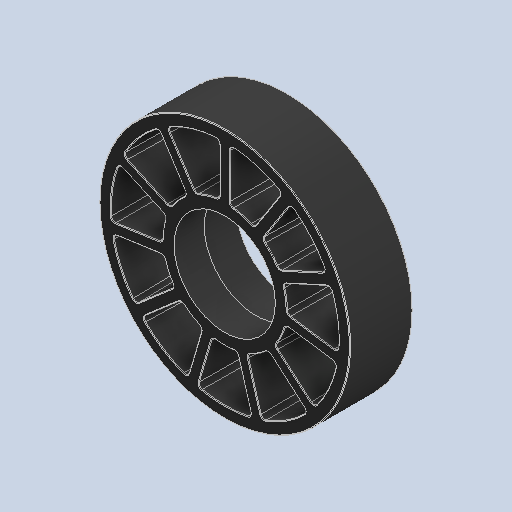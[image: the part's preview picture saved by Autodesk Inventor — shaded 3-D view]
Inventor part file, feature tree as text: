
AUTODESK INVENTOR PART (.ipt)
format: ipt  version: 2023.4 (Build 274418000, 418)  size: 1,051,648 bytes
history: native  units: in
note: dims shown in document units (in); Inventor stores cm internally (conversion verified against a paired STEP export)
features: fillet x1
ambient origin geometry x8: Origin, YZ Plane, XZ Plane, XY Plane, X Axis, Y Axis, Z Axis, Center Point
bodies: Solid1 (feature_tree)
feature tree (1):
  fillet  "Fillet2"  [1 undecoded]
note: 1 required parameter value undecoded (feature->parameter linkage not recoverable at this tier; creation-order binding heuristic only, values carry confidence <= 0.55)
